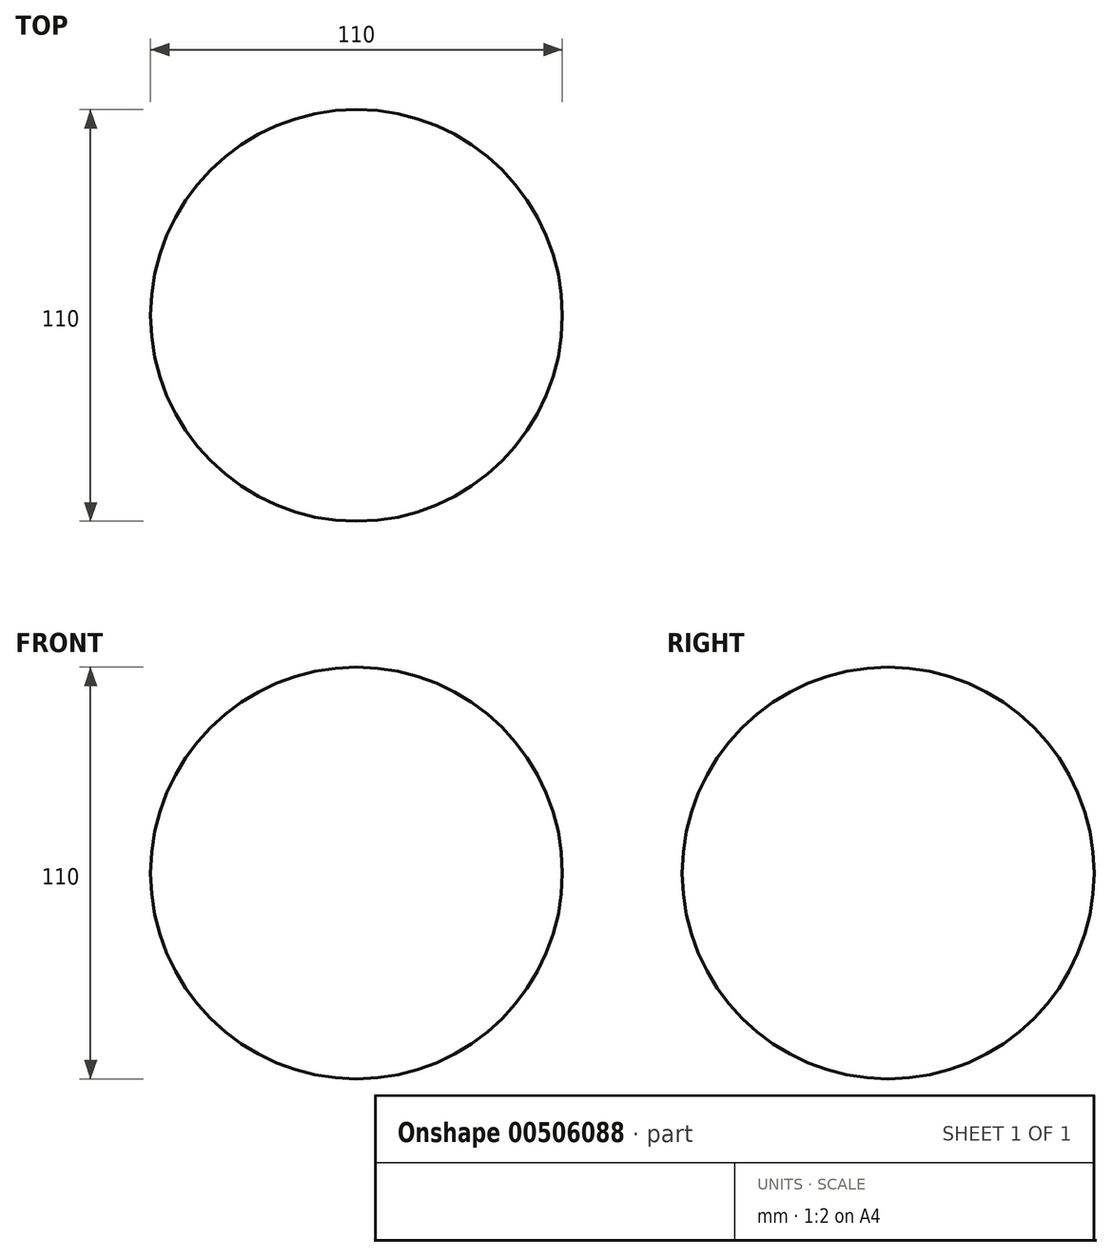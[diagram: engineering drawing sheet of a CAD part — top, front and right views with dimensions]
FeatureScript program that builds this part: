
annotation { "Feature Type Name" : "Feature", "Feature Type Description" : "" }
export const myFeature = defineFeature(function(context is Context, id is Id, definition is map)
    precondition{}
    {
        {
            var Q0;
            Q0=qCreatedBy(makeId("Front.planeOp"),FACE);
            var sketch = newSketch(context, id + "F0", { "sketchPlane" : qUnion([Q0])});
            skLineSegment(sketch, "E0", {"start": v(0, 55) * mm, "end": v(0, -55) * mm});
            skArc(sketch, "E1", {"start": v(0, -55) * mm, "mid": v(55, 0) * mm, "end": v(0, 55) * mm});
            skSolve(sketch);
        }
        {
            var Q0;
            Q0 = qSketchRegion(id + "F0", true);
            var Q1;
            Q1=sQuery(id+"F0.wireOp",EDGE,"E0");
            revolve(context, id + "F1", {"entities" : qUnion([Q0]), "axis" : qUnion([Q1]), "revolveType" : RevolveType.FULL});
        }
    });
